# Revit family: Door-Access-Cendrex-Fire_Rated_Insulated_Upward_Opening-PFU
name_source: partatom
category: Specialty Equipment
revit_build: Autodesk Revit Architecture 2013 (Build: 20130531_2115(x64)
units: mm (PartAtom-declared; Revit-internal decimal feet)

## types (4) — shared parameters
Assembly Code = C1020700
Available Options = http://cendrex.com
Cendrex LEED Ready Program = http://www.cendrex.com
Construction Material = Metal - Cendrex - Aluminum
Default Elevation = 0"
Description = Fire Rated Insulated Upward Opening Access Door for Ceiling
Door Open = No
Door Swing = 0.00°
Finish = Metal - Cendrex - Powder Coated White
Frame Depth = 2 7/8"
Manufacturer = Cendrex
Model = PFU
Product Documentation Link = http://cendrex.com
Product Page URL = http://cendrex.com
URL = http://www.cendrex.com

## per-type parameters (varying)
| type | Door Height | Door Width | Frame Height | Frame Width | Height Calc | Width Calc |
| Custom | 12" | 12" | 14 1/4" | 14 1/4" | 12" | 12" |
| 22x30 | 30" | 22" | 32 1/4" | 24 1/4" | 30" | 22" |
| 22x36 | 36" | 22" | 38 1/4" | 24 1/4" | 36" | 22" |
| 24x24 | 24" | 24" | 26 1/4" | 26 1/4" | 24" | 24" |

## geometry (parser evidence)
native form markers: Blend x24, Sweep x19
no freeform markers — native parametric forms only
